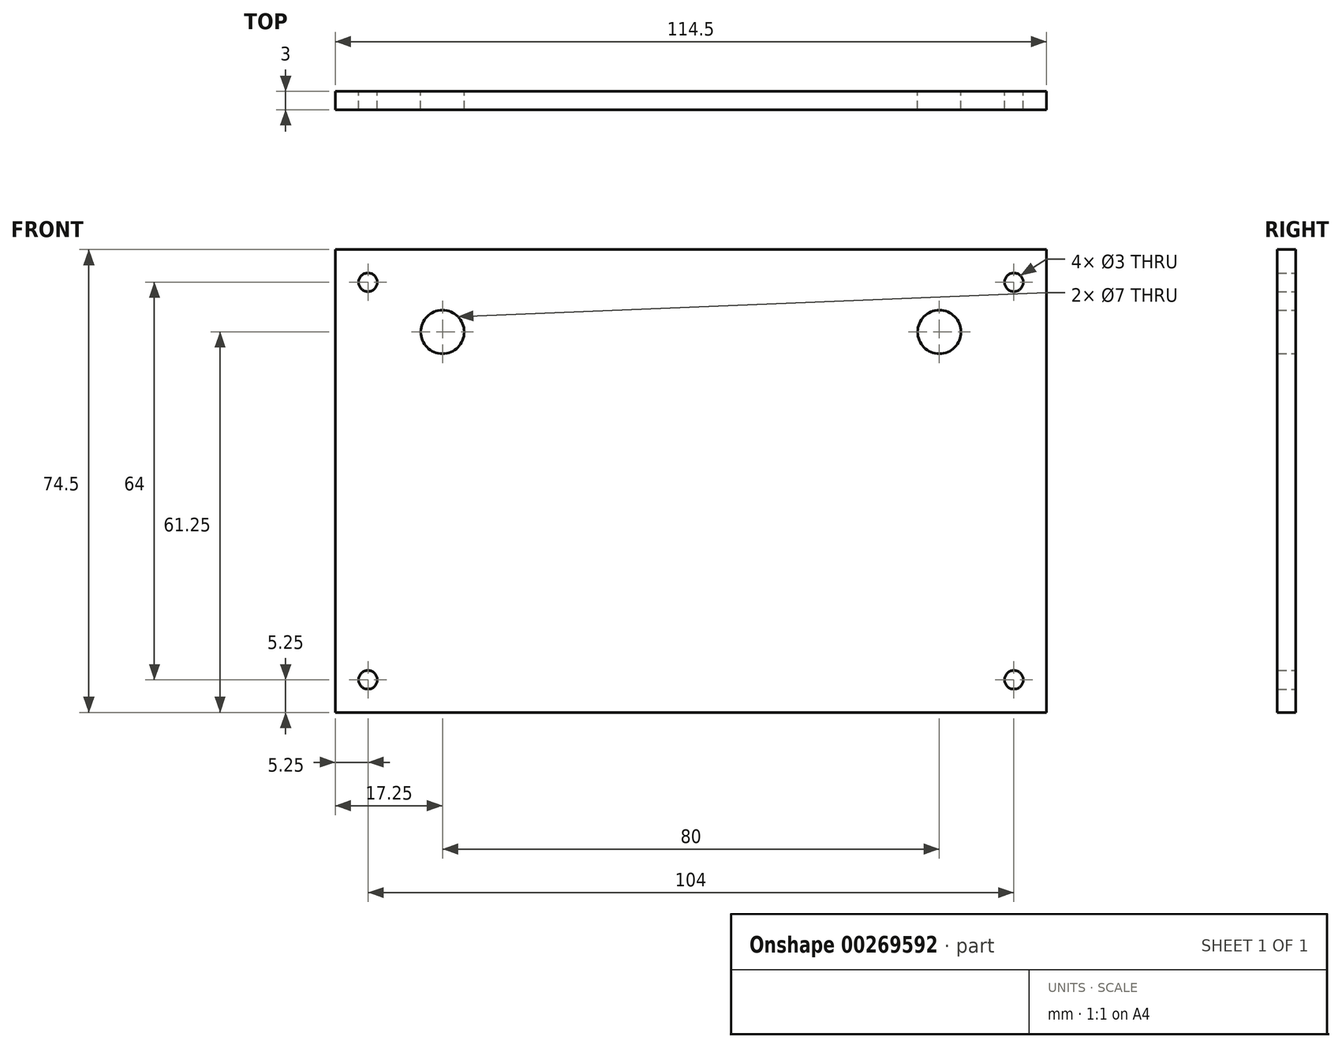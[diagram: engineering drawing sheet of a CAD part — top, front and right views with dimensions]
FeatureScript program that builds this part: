
annotation { "Feature Type Name" : "Feature", "Feature Type Description" : "" }
export const myFeature = defineFeature(function(context is Context, id is Id, definition is map)
    precondition{}
    {
        {
            var Q0;
            Q0=qCreatedBy(makeId("Front.planeOp"),FACE);
            var sketch = newSketch(context, id + "F0", { "sketchPlane" : qUnion([Q0])});
            skLineSegment(sketch, "E0.bottom", {"start": v(-57.25, 37.25) * mm, "end": v(57.25, 37.25) * mm});
            skLineSegment(sketch, "E0.top", {"start": v(-57.25, -37.25) * mm, "end": v(57.25, -37.25) * mm});
            skLineSegment(sketch, "E0.left", {"start": v(-57.25, 37.25) * mm, "end": v(-57.25, -37.25) * mm});
            skLineSegment(sketch, "E0.right", {"start": v(57.25, 37.25) * mm, "end": v(57.25, -37.25) * mm});
            skPoint(sketch, "E0.middle", {"position": v(0, 0) * mm});
            skCircle(sketch, "E1", {"center": v(-52, 32) * mm, "radius": 1.5 * mm});
            skCircle(sketch, "E2.0.1.0", {"center": v(-52, -32) * mm, "radius": 1.5 * mm});
            skCircle(sketch, "E2.1.0.0", {"center": v(52, 32) * mm, "radius": 1.5 * mm});
            skCircle(sketch, "E2.1.1.0", {"center": v(52, -32) * mm, "radius": 1.5 * mm});
            skLineSegment(sketch, "E2.direction1", {"start": v(-52, 32) * mm, "end": v(52, 32) * mm, "construction": true});
            skLineSegment(sketch, "E2.direction2", {"start": v(-52, 32) * mm, "end": v(-52, -32) * mm, "construction": true});
            skCircle(sketch, "E3", {"center": v(-40, 24) * mm, "radius": 3.5 * mm});
            skCircle(sketch, "E4.1.0.0", {"center": v(40, 24) * mm, "radius": 3.5 * mm});
            skLineSegment(sketch, "E4.direction1", {"start": v(-40, 24) * mm, "end": v(40, 24) * mm, "construction": true});
            skSolve(sketch);
        }
        {
            var Q0;
            Q0 = qSketchRegion(id + "F0", true);
            extrude(context, id + "F1", {"entities" : qUnion([Q0]), "depth" : 3 * mm});
        }
    });
